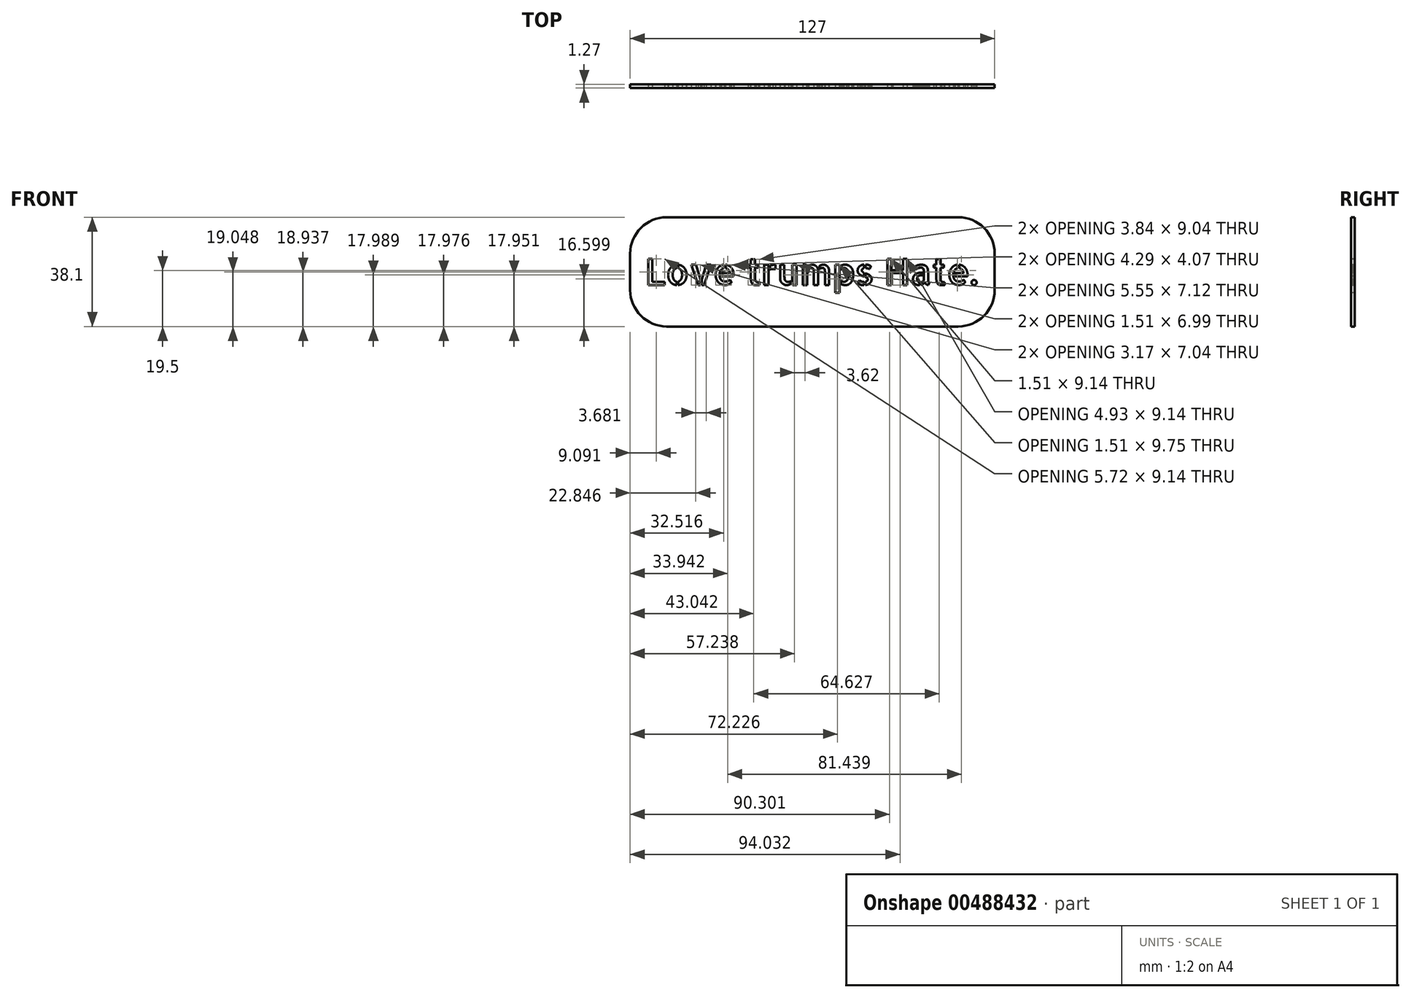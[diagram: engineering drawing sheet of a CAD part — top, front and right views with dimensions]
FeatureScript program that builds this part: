
annotation { "Feature Type Name" : "Feature", "Feature Type Description" : "" }
export const myFeature = defineFeature(function(context is Context, id is Id, definition is map)
    precondition{}
    {
        {
            var Q0;
            Q0=qCreatedBy(makeId("Front.planeOp"),FACE);
            var sketch = newSketch(context, id + "F0", { "sketchPlane" : qUnion([Q0])});
            skLineSegment(sketch, "E0.bottom", {"start": v(0, 0) * mm, "end": v(-127, 0) * mm});
            skLineSegment(sketch, "E0.top", {"start": v(0, 38.1) * mm, "end": v(-127, 38.1) * mm});
            skLineSegment(sketch, "E0.left", {"start": v(0, 0) * mm, "end": v(0, 38.1) * mm});
            skLineSegment(sketch, "E0.right", {"start": v(-127, 0) * mm, "end": v(-127, 38.1) * mm});
            skSolve(sketch);
        }
        {
            var Q0;
            Q0 = qSketchRegion(id + "F0", true);
            extrude(context, id + "F1", {"entities" : qUnion([Q0]), "depth" : 1.27 * mm});
        }
        {
            var Q0;
            Q0=makeQuery(id+"F1.opExtrude","SWEPT_EDGE",EDGE,{"disambiguationData":[OSD([sQuery(id+"F0.wireOp",EDGE,"E0.top"),sQuery(id+"F0.wireOp",EDGE,"E0.right")])]});
            var Q1;
            Q1=makeQuery(id+"F1.opExtrude","SWEPT_EDGE",EDGE,{"disambiguationData":[OSD([sQuery(id+"F0.wireOp",EDGE,"E0.bottom"),sQuery(id+"F0.wireOp",EDGE,"E0.right")])]});
            var Q2;
            Q2=makeQuery(id+"F1.opExtrude","SWEPT_EDGE",EDGE,{"disambiguationData":[OSD([sQuery(id+"F0.wireOp",EDGE,"E0.top"),sQuery(id+"F0.wireOp",EDGE,"E0.left")])]});
            var Q3;
            Q3=makeQuery(id+"F1.opExtrude","SWEPT_EDGE",EDGE,{"disambiguationData":[OSD([sQuery(id+"F0.wireOp",EDGE,"E0.bottom"),sQuery(id+"F0.wireOp",EDGE,"E0.left")])]});
            fillet(context, id + "F2", {"entities" : qUnion([Q0, Q1, Q2, Q3]), "radius" : 12.7 * mm, "tangentPropagation" : true, "allowEdgeOverflow" : false});
        }
        {
            var Q0;
            Q0=makeQuery(id+"F1.opExtrude","CAP_FACE",FACE,{"disambiguationData":[OSD([sQuery(id+"F0.wireOp",EDGE,"E0.bottom"),sQuery(id+"F0.wireOp",EDGE,"E0.top"),sQuery(id+"F0.wireOp",EDGE,"E0.left"),sQuery(id+"F0.wireOp",EDGE,"E0.right")])],"isStart":false});
            var sketch = newSketch(context, id + "F3", { "sketchPlane" : qUnion([Q0])});
            skText(sketch, "E1", { "text": "Love trumps Hate.", "fontName": "AllertaStencil-Regular.ttf"});
            const initialGuessF3  = {"E1": [-0.12192, 0.01448, 1, 0, 0.00914]};
            skSetInitialGuess(sketch, initialGuessF3);
            skSolve(sketch);
        }
        {
            var Q0;
            Q0 = qSketchRegion(id + "F3", true);
            extrude(context, id + "F4", {"entities" : qUnion([Q0]), "operationType" : NewBodyOperationType.REMOVE, "endBound" : BoundingType.THROUGH_ALL, "oppositeDirection" : true, "depth" : 25.4 * mm});
        }
    });
